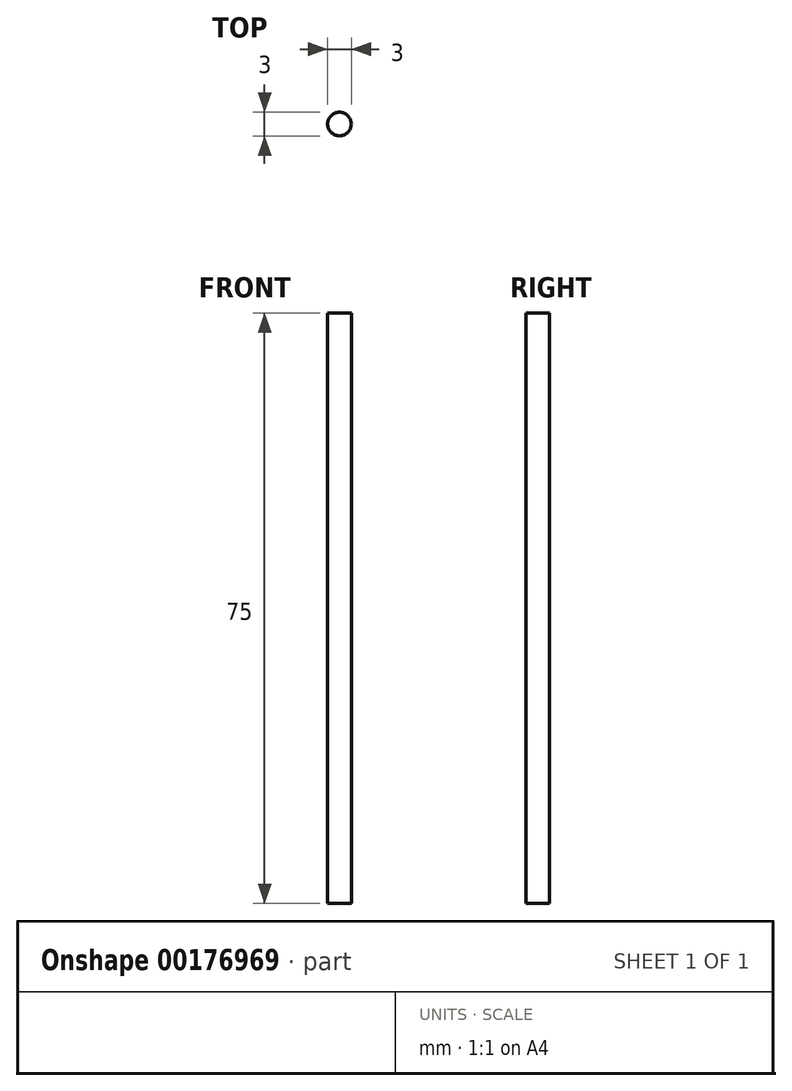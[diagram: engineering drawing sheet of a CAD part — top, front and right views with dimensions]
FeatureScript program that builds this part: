
annotation { "Feature Type Name" : "Feature", "Feature Type Description" : "" }
export const myFeature = defineFeature(function(context is Context, id is Id, definition is map)
    precondition{}
    {
        {
            var Q0;
            Q0=qCreatedBy(makeId("Top.planeOp"),FACE);
            var sketch = newSketch(context, id + "F0", { "sketchPlane" : qUnion([Q0])});
            skCircle(sketch, "E0", {"center": v(0, 0) * mm, "radius": 1.5 * mm});
            skSolve(sketch);
        }
        {
            var Q0;
            Q0=makeQuery(id+"F0.imprint","IMPRINT",FACE,{"disambiguationData":[TD([[makeQuery(id+"F0.imprint","IMPRINT",EDGE,{"derivedFrom":sQuery(id+"F0.wireOp",EDGE,"E0")}),1.0]])]});
            extrude(context, id + "F1", {"entities" : qUnion([Q0]), "depth" : 50 * mm, "hasSecondDirection" : true, "secondDirectionOppositeDirection" : true, "secondDirectionDepth" : 25 * mm});
        }
    });
